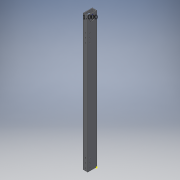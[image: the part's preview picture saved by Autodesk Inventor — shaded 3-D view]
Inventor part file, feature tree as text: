
AUTODESK INVENTOR PART (.ipt)
format: ipt  version: 2018 (Build 220112000, 112)  size: 195,584 bytes
history: native  units: in
note: dims shown in document units (in); Inventor stores cm internally (conversion verified against a paired STEP export)
features: sketch x6, extrude x5
ambient origin geometry x8: Origin, YZ Plane, XZ Plane, XY Plane, X Axis, Y Axis, Z Axis, Center Point
bodies: Solid1 (feature_tree)
feature tree (11):
  extrude  "Extrusion1"  Depth=2.0in
  extrude  "Extrusion3"  Depth=30.0in TaperAngle=0.0deg
  sketch  "Sketch4"  dims[d19=0.5in d20=1.0in]
  extrude  "Extrusion4"  Depth=1.0in
  extrude  "Extrusion5"  Depth=1.0in
  extrude  "Extrusion6"  Depth=0.2031in
  sketch  "Sketch1"  dims[d0=1.0in d1=2.0in]
  sketch  "Sketch3"  dims[d2=0.125in d3=30.0in d4=0.0in]
  sketch  "Sketch5"  dims[d21=1.0in d22=0.2031in]
  sketch  "Sketch6"  dims[d23=0.2031in d24=0.2031in]
  sketch  "Sketch7"  dims[d30=30.0in d31=0.0in d38=0.5in d39=0.2031in d40=1.0in d41=1.0in d42=0.2031in d43=0.2031in d44=1.0in d46=0.5in d47=0.5in d48=0.2031in d49=0.2031in d50=0.2031in d51=0.5in d52=0.5in d53=0.5in d54=0.2031in d55=0.2031in d56=0.2031in d57=30.0in d58=0.0in d59=1.0in d60=1.125in d61=12.0in d62=0.0in d63=4.0in d64=7.0in d65=1.0in d66=1.0in d67=0.2031in d68=0.2031in d69=0.2031in d70=0.2031in d71=2.0in d72=0.0in]
